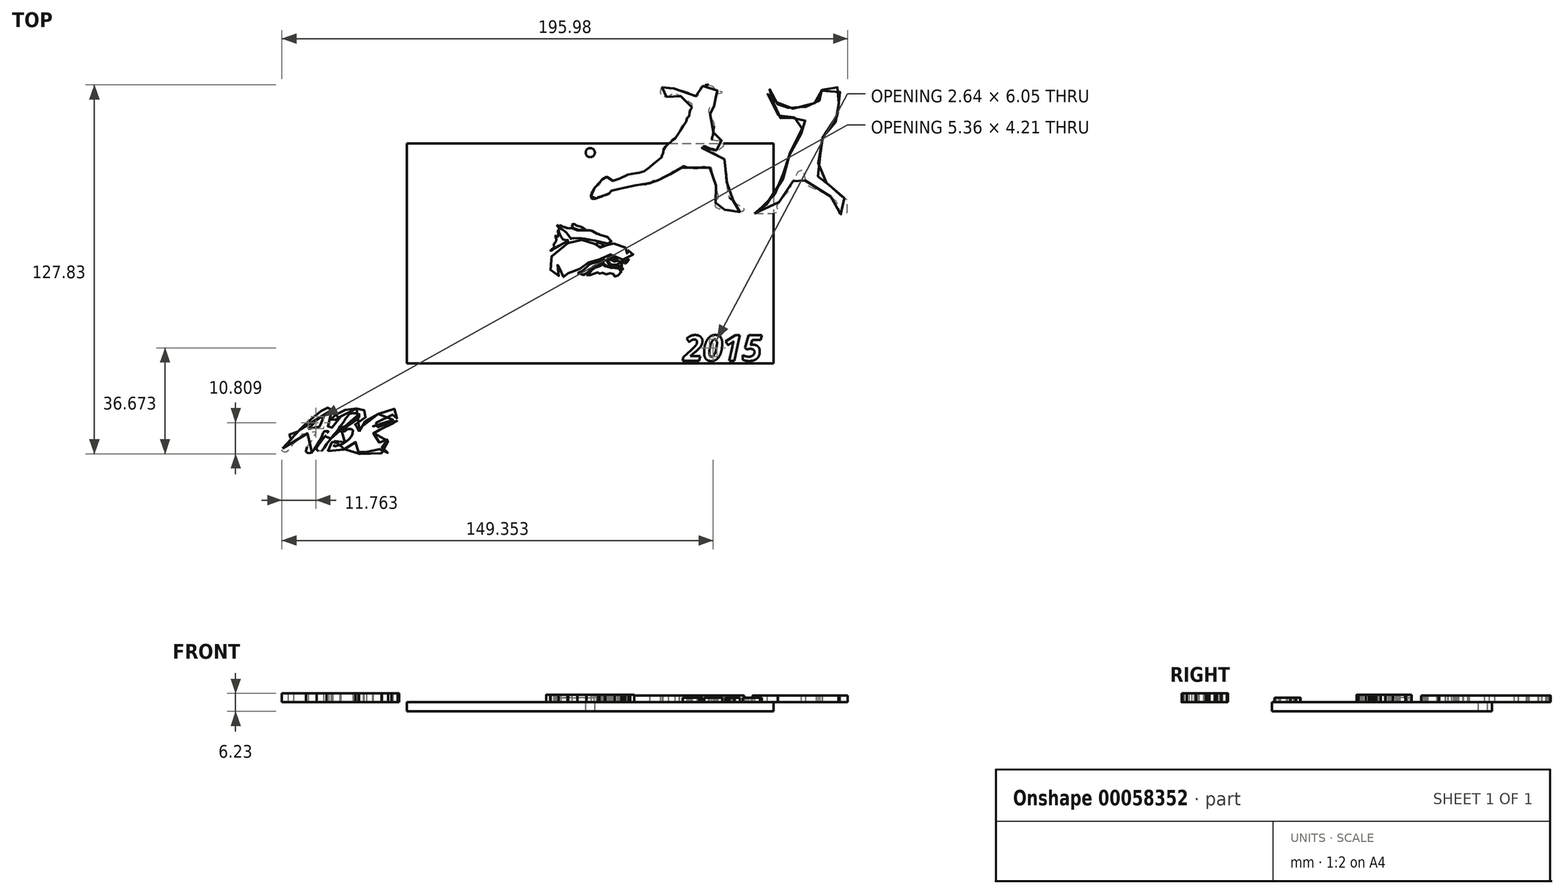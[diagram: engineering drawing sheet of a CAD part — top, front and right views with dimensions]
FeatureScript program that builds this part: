
annotation { "Feature Type Name" : "Feature", "Feature Type Description" : "" }
export const myFeature = defineFeature(function(context is Context, id is Id, definition is map)
    precondition{}
    {
        {
            var Q0;
            Q0=qCreatedBy(makeId("Top.planeOp"),FACE);
            var sketch = newSketch(context, id + "F0", { "sketchPlane" : qUnion([Q0])});
            skFitSpline(sketch, "E0", {"points": [v(-30.29, 18.5) * mm, v(-33.5, 18.37) * mm, v(-36.8, 18.87) * mm, v(-39.5, 22) * mm, v(-42.22, 26.8) * mm, v(-43.58, 30.51) * mm, v(-43.65, 32.58) * mm, v(-43.94, 32.87) * mm, v(-44.5, 32.87) * mm, v(-44.44, 31.3) * mm, v(-44.22, 23) * mm, v(-44.44, 22.72) * mm, v(-45.3, 23.3) * mm, v(-47.3, 24.5) * mm, v(-48.36, 24.87) * mm, v(-48.22, 23.58) * mm, v(-48.22, 21.87) * mm, v(-46.94, 20.08) * mm, v(-45.86, 19.3) * mm, v(-50.65, 12.94) * mm, v(-50.72, 12) * mm, v(-50.5, 10.86) * mm, v(-50, 10.08) * mm, v(-49.58, 9.15) * mm, v(-49.86, 8.65) * mm, v(-51.87, 7) * mm, v(-54.65, 4.8) * mm, v(-55.3, 3.86) * mm, v(-55.08, 3.3) * mm, v(-54.37, 3.15) * mm, v(-53.22, 4.58) * mm, v(-47.65, 8.15) * mm, v(-38.8, 12.86) * mm, v(-32.3, 16.37) * mm, v(-30.22, 17.3) * mm, v(-30.29, 18.5) * mm]});
            skFitSpline(sketch, "E1", {"points": [v(-45.56, 38.1) * mm, v(-39.19, 33.33) * mm, v(-33.89, 30.17) * mm, v(-33.2, 29.53) * mm, v(-32.34, 28.09) * mm, v(-27.47, 21.24) * mm, v(-26.61, 20.27) * mm, v(-25.17, 20.49) * mm, v(-18.42, 21.13) * mm, v(-14.2, 21.18) * mm, v(-7.5, 20.17) * mm, v(5.34, 17.86) * mm, v(14.44, 15.94) * mm, v(23.65, 13.64) * mm, v(24.13, 13.48) * mm, v(24.98, 14.01) * mm, v(27.55, 15.35) * mm, v(28.78, 16.2) * mm, v(28.94, 17) * mm, v(28.2, 17.92) * mm, v(26.54, 19.74) * mm, v(24.82, 21.66) * mm, v(24.23, 22.36) * mm, v(23.16, 22.84) * mm, v(15.46, 24.93) * mm, v(12.25, 26.43) * mm, v(8.77, 27.71) * mm, v(5.02, 29.96) * mm, v(2.72, 31.14) * mm, v(0.58, 31.67) * mm, v(-0.97, 31.94) * mm, v(-11.04, 31.83) * mm, v(-16.17, 31.78) * mm, v(-17.14, 31.67) * mm, v(-17.94, 32.05) * mm, v(-21.42, 33.39) * mm, v(-25.06, 34.62) * mm, v(-25.86, 34.94) * mm, v(-33.03, 35) * mm, v(-35.17, 36.06) * mm, v(-37.2, 36.97) * mm, v(-39.78, 38.1) * mm, v(-42.5, 38.52) * mm, v(-44.65, 38.8) * mm, v(-45.5, 38.8) * mm, v(-45.56, 38.1) * mm]});
            skFitSpline(sketch, "E2", {"points": [v(-25.5, 39.45) * mm, v(-23.8, 35.5) * mm, v(-23.6, 34.96) * mm, v(-23.33, 34.6) * mm, v(-22.32, 34.5) * mm, v(-20.87, 34.29) * mm, v(-19.32, 33.82) * mm, v(-17, 32.8) * mm, v(-16.66, 32.64) * mm, v(-10.29, 32.57) * mm, v(-6.4, 32.74) * mm, v(-7.55, 33.78) * mm, v(-9.88, 35.44) * mm, v(-12.4, 36.65) * mm, v(-15.28, 37.53) * mm, v(-17.5, 38.13) * mm, v(-19.25, 38.64) * mm, v(-20.47, 39.55) * mm, v(-22.29, 40.72) * mm, v(-24.82, 40.36) * mm, v(-25.5, 39.95) * mm, v(-25.5, 39.45) * mm]});
            skFitSpline(sketch, "E3", {"points": [v(9.56, 14.74) * mm, v(8.97, 13.48) * mm, v(9.05, 12.11) * mm, v(10.1, 10.97) * mm, v(11.96, 9.82) * mm, v(13.28, 9.39) * mm, v(15.02, 9.41) * mm, v(15.96, 9.87) * mm, v(16.9, 10.71) * mm, v(18.18, 11.63) * mm, v(18.5, 12.04) * mm, v(18.53, 12.75) * mm, v(17.31, 13.08) * mm, v(12.77, 14.38) * mm, v(10.8, 15.05) * mm, v(10.02, 15.07) * mm, v(9.56, 14.74) * mm]});
            skFitSpline(sketch, "E4", {"points": [v(-17.1, -27.56) * mm, v(-14.32, -28.36) * mm, v(-10.42, -29.66) * mm, v(-9.47, -30) * mm, v(-8.36, -29.36) * mm, v(-5.11, -27.03) * mm, v(-3.7, -26.1) * mm, v(-1.71, -24.39) * mm, v(1.04, -21.14) * mm, v(2.6, -19.5) * mm, v(4.48, -18.2) * mm, v(8.18, -16.48) * mm, v(11.2, -15.6) * mm, v(13.42, -14.95) * mm, v(16.82, -13.3) * mm, v(16.9, -11.82) * mm, v(17.12, -10.02) * mm, v(17.89, -8.3) * mm, v(18.46, -7.46) * mm, v(17.39, -7.85) * mm, v(16.2, -8.76) * mm, v(14.6, -9.87) * mm, v(7.8, -12.43) * mm, v(2.34, -13.8) * mm, v(-0.68, -15.03) * mm, v(-3.43, -17.63) * mm, v(-7.79, -21.49) * mm, v(-10.58, -23.59) * mm, v(-14.93, -25.92) * mm, v(-17.6, -26.83) * mm, v(-17.1, -27.56) * mm]});
            skFitSpline(sketch, "E5", {"points": [v(23.75, -4.13) * mm, v(24.48, -3.2) * mm, v(25.16, -3.08) * mm, v(26.69, -2.9) * mm, v(28.06, -2.89) * mm, v(29.84, -3.32) * mm, v(32.15, -4.32) * mm, v(34.8, -5.67) * mm, v(37.04, -6.9) * mm, v(37.75, -7.35) * mm, v(37.56, -7.75) * mm, v(36.27, -8.6) * mm, v(35.24, -9) * mm, v(33.8, -8.72) * mm, v(32.37, -8.25) * mm, v(31.43, -7.95) * mm, v(31.25, -7.13) * mm, v(31.15, -6.36) * mm, v(31.15, -5.14) * mm, v(30.8, -5.42) * mm, v(30.14, -6) * mm, v(29.88, -6.36) * mm, v(29.28, -6.34) * mm, v(27.8, -6.36) * mm, v(27.07, -6.34) * mm, v(27.1, -5.97) * mm, v(27.2, -5.35) * mm, v(27.48, -4.56) * mm, v(27.63, -3.85) * mm, v(26.56, -3.87) * mm, v(24.78, -4.17) * mm, v(23.75, -4.13) * mm]});
            skFitSpline(sketch, "E6", {"points": [v(42.3, -15.24) * mm, v(43.14, -12.43) * mm, v(44, -9.41) * mm, v(44.24, -9.4) * mm, v(46.02, -9.52) * mm, v(48.6, -9.68) * mm, v(50.5, -9.46) * mm, v(51.99, -8.83) * mm, v(53.36, -8.48) * mm, v(53.14, -8.89) * mm, v(51.38, -11.46) * mm, v(50.37, -12.5) * mm, v(49.3, -13.46) * mm, v(47.98, -14.1) * mm, v(47.94, -13.77) * mm, v(48.02, -12.17) * mm, v(48.08, -10.9) * mm, v(47.84, -10.97) * mm, v(46.36, -12.39) * mm, v(43.91, -14.31) * mm, v(42.3, -15.24) * mm]});
            skFitSpline(sketch, "E7", {"points": [v(43.59, -15.91) * mm, v(42.43, -17.19) * mm, v(42.33, -17.35) * mm, v(42.48, -17.57) * mm, v(43.59, -18.48) * mm, v(43.75, -18.58) * mm, v(43.77, -18.3) * mm, v(43.77, -16.05) * mm, v(43.75, -15.86) * mm, v(43.59, -15.91) * mm]});
            skFitSpline(sketch, "E8", {"points": [v(39.9, -15.52) * mm, v(40.03, -16.05) * mm, v(40.03, -17.43) * mm, v(39.79, -18.75) * mm, v(39.3, -19.6) * mm, v(38.94, -19.62) * mm, v(37.16, -19.62) * mm, v(36.97, -19.6) * mm, v(37.16, -19.2) * mm, v(39.64, -15.72) * mm, v(39.9, -15.52) * mm]});
            skFitSpline(sketch, "E9", {"points": [v(41.04, -17.52) * mm, v(40.6, -19.86) * mm, v(40.58, -20.2) * mm, v(40.94, -20.3) * mm, v(41.42, -20.36) * mm, v(42.17, -20.96) * mm, v(43.1, -21.76) * mm, v(43.54, -22.48) * mm, v(43.78, -22.82) * mm, v(44.22, -22.62) * mm, v(45.2, -22.02) * mm, v(45.56, -21.78) * mm, v(45.4, -21.42) * mm, v(43.85, -19.47) * mm, v(42.58, -18.41) * mm, v(41.47, -17.62) * mm, v(41.04, -17.52) * mm]});
            skFitSpline(sketch, "E10", {"points": [v(23.28, -8.71) * mm, v(24.22, -9.48) * mm, v(25, -10.64) * mm, v(25.95, -12.13) * mm, v(26.6, -13.31) * mm, v(27.4, -14.2) * mm, v(28.72, -15) * mm, v(29.97, -15.52) * mm, v(32.5, -15.81) * mm, v(35.48, -15.62) * mm, v(37.62, -15.28) * mm, v(38.1, -15.21) * mm, v(38.49, -14.78) * mm, v(38.97, -14.27) * mm, v(39.02, -13.82) * mm, v(39.64, -13.26) * mm, v(40.32, -12.9) * mm, v(41.01, -12.37) * mm, v(41.6, -11.58) * mm, v(41.16, -11.34) * mm, v(37.98, -10.3) * mm, v(37.3, -10.13) * mm, v(36.37, -10.42) * mm, v(35, -10.93) * mm, v(34.1, -11.31) * mm, v(33.5, -11.31) * mm, v(32.71, -10.93) * mm, v(32.33, -10.78) * mm, v(29.77, -9.68) * mm, v(27.85, -8.71) * mm, v(26.3, -8.06) * mm, v(25, -7.8) * mm, v(23.78, -7.65) * mm, v(23.13, -7.7) * mm, v(22.9, -8.16) * mm, v(23.28, -8.71) * mm]});
            skFitSpline(sketch, "E11", {"points": [v(37.12, -17.57) * mm, v(36.2, -18.77) * mm, v(36, -19.06) * mm, v(35.65, -19.01) * mm, v(33.31, -19) * mm, v(30.14, -18.85) * mm, v(27.56, -18.41) * mm, v(24.65, -17.84) * mm, v(22.36, -16.92) * mm, v(20.39, -15.74) * mm, v(19.35, -14.61) * mm, v(18.56, -13.2) * mm, v(18.15, -11.77) * mm, v(18.22, -10.25) * mm, v(18.6, -9.72) * mm, v(19.64, -9.2) * mm, v(20.97, -9.12) * mm, v(22.53, -10.1) * mm, v(23.61, -11.58) * mm, v(24.5, -13.36) * mm, v(25.76, -15.48) * mm, v(27.2, -16.44) * mm, v(28.9, -17.11) * mm, v(31.03, -17.5) * mm, v(33.8, -17.55) * mm, v(36.47, -17.6) * mm, v(37.12, -17.57) * mm]});
            skFitSpline(sketch, "E12", {"points": [v(-5.34, -30.01) * mm, v(-4.04, -29.3) * mm, v(-1.91, -27.92) * mm, v(-0.65, -27.02) * mm, v(1.3, -24.68) * mm, v(2.41, -23.09) * mm, v(3.79, -21.43) * mm, v(4.8, -20.5) * mm, v(7.54, -19.23) * mm, v(10.28, -18.5) * mm, v(12.8, -17.86) * mm, v(14.82, -17.21) * mm, v(16.33, -16.24) * mm, v(17.63, -15.12) * mm, v(18.1, -15.37) * mm, v(19.54, -16.63) * mm, v(23.37, -18.5) * mm, v(27.08, -19.66) * mm, v(31.16, -20.24) * mm, v(33.54, -20.35) * mm, v(36.06, -20.5) * mm, v(38.08, -20.78) * mm, v(41.04, -21.68) * mm, v(42.44, -23.38) * mm, v(42.84, -25.69) * mm, v(41.76, -28.03) * mm, v(39.56, -29.83) * mm, v(36.13, -31.53) * mm, v(33.82, -32.57) * mm, v(33.97, -31.96) * mm, v(34.04, -30.37) * mm, v(33.5, -29.22) * mm, v(32.24, -28.4) * mm, v(30.43, -27.78) * mm, v(29.68, -27.74) * mm, v(27.44, -27.34) * mm, v(25.2, -27.74) * mm, v(22.93, -28.4) * mm, v(21.56, -29.22) * mm, v(21.2, -29.8) * mm, v(20.48, -29.76) * mm, v(20.52, -29.11) * mm, v(20.3, -27.85) * mm, v(19.54, -27.13) * mm, v(18.07, -26.77) * mm, v(16.66, -26.73) * mm, v(15.32, -27.02) * mm, v(13.74, -27.63) * mm, v(12.48, -28.35) * mm, v(11.61, -28.75) * mm, v(11.29, -28.5) * mm, v(11.47, -28) * mm, v(12.04, -27.3) * mm, v(12.48, -26.8) * mm, v(12.37, -26.37) * mm, v(11.75, -26.12) * mm, v(10.7, -26.15) * mm, v(9.7, -26.33) * mm, v(8.18, -26.84) * mm, v(5.4, -27.92) * mm, v(3, -28.9) * mm, v(0.61, -29.76) * mm, v(-1.44, -30.09) * mm, v(-4.18, -30.34) * mm, v(-5.34, -30.01) * mm]});
            skFitSpline(sketch, "E13", {"points": [v(-53.65, -9.02) * mm, v(-54.94, -12.28) * mm, v(-55.45, -15.2) * mm, v(-55.62, -18.54) * mm, v(-55.45, -21.37) * mm, v(-54.5, -23.77) * mm, v(-51.76, -26.7) * mm, v(-49.45, -28.58) * mm, v(-46.02, -30.38) * mm, v(-43.7, -31.32) * mm, v(-44.05, -30.38) * mm, v(-45.67, -26.95) * mm, v(-46.62, -23.26) * mm, v(-46.79, -19.23) * mm, v(-45.16, -15.45) * mm, v(-43.53, -13.74) * mm, v(-41.73, -12.2) * mm, v(-40.96, -11.77) * mm, v(-41.64, -13.74) * mm, v(-43.27, -19.14) * mm, v(-43.7, -23.43) * mm, v(-42.84, -26.7) * mm, v(-40.87, -29.7) * mm, v(-38.04, -32.18) * mm, v(-35.04, -33.8) * mm, v(-30.75, -35.48) * mm, v(-31.27, -34.32) * mm, v(-31.7, -31.66) * mm, v(-30.75, -27.98) * mm, v(-28.86, -25.49) * mm, v(-24.32, -23.95) * mm, v(-18.31, -22.66) * mm, v(-14.28, -21.37) * mm, v(-12.83, -20.43) * mm, v(-11.02, -18.46) * mm, v(-8.2, -15.88) * mm, v(-4.76, -13.48) * mm, v(-1.08, -12.1) * mm, v(2.96, -11.08) * mm, v(7.33, -10.14) * mm, v(10.85, -9.1) * mm, v(13.85, -7.56) * mm, v(17.1, -5.25) * mm, v(19.94, -3.28) * mm, v(22.77, -1.47) * mm, v(28.51, -1.39) * mm, v(32.2, -2.68) * mm, v(38.12, -5.33) * mm, v(43.18, -7.74) * mm, v(47.04, -8.68) * mm, v(50.39, -8.34) * mm, v(55.19, -6.45) * mm, v(58.02, -3.96) * mm, v(60.44, 0.75) * mm, v(60.82, 2.12) * mm, v(59.83, 2.66) * mm, v(55.54, 4.5) * mm, v(53.37, 5.11) * mm, v(53.12, 4.79) * mm, v(52.76, 3.5) * mm, v(52.11, 1.5) * mm, v(52.3, 1.11) * mm, v(54.93, -1.09) * mm, v(55.14, -1.49) * mm, v(55.1, -1.63) * mm, v(54.7, -1.3) * mm, v(51, 0) * mm, v(51.07, 0.64) * mm, v(51.35, 3.27) * mm, v(51.54, 5.44) * mm, v(51.79, 6.38) * mm, v(51.46, 7.02) * mm, v(50.96, 7.53) * mm, v(49.73, 7.78) * mm, v(43.02, 9.15) * mm, v(37.47, 10.52) * mm, v(35.42, 11.6) * mm, v(33.14, 12.87) * mm, v(30.87, 14.7) * mm, v(30.26, 15.07) * mm, v(29.65, 14.85) * mm, v(28.7, 14.13) * mm, v(25.54, 11.53) * mm, v(25.17, 11.24) * mm, v(24.67, 11.2) * mm, v(23.48, 11.71) * mm, v(22, 12.15) * mm, v(21.64, 12.22) * mm, v(20.96, 11.68) * mm, v(19.4, 10.13) * mm, v(17.13, 9) * mm, v(14.97, 8.1) * mm, v(11, 8.03) * mm, v(8.12, 8.86) * mm, v(6.06, 10.52) * mm, v(5.09, 11.46) * mm, v(4.87, 11.9) * mm, v(5.09, 12.25) * mm, v(7.04, 14.16) * mm, v(8, 15.14) * mm, v(8.23, 15.46) * mm, v(7.76, 15.68) * mm, v(-7.9, 18.1) * mm, v(-15.86, 18.85) * mm, v(-22.35, 18.89) * mm, v(-26, 17.77) * mm, v(-34.22, 11.96) * mm, v(-41.25, 6.3) * mm, v(-52.68, -3.25) * mm, v(-60.18, -9.64) * mm, v(-61.23, -10.65) * mm, v(-60.4, -10.6) * mm, v(-54.16, -9.02) * mm, v(-53.65, -9.02) * mm]});
            skSolve(sketch);
        }
        {
            var Q0;
            Q0 = qSketchRegion(id + "F0", true);
            extrude(context, id + "F1", {"entities" : qUnion([Q0]), "depth" : 10.16 * mm});
        }
        {
            var Q0;
            Q0=makeQuery(id+"F1.opExtrude","SWEPT_BODY",BODY,{"disambiguationData":[OSD([sQuery(id+"F0.wireOp",EDGE,"E8")])]});
            var Q1;
            Q1=makeQuery(id+"F1.opExtrude","SWEPT_BODY",BODY,{"disambiguationData":[OSD([sQuery(id+"F0.wireOp",EDGE,"E13")])]});
            var Q2;
            Q2=makeQuery(id+"F1.opExtrude","SWEPT_BODY",BODY,{"disambiguationData":[OSD([sQuery(id+"F0.wireOp",EDGE,"E9")])]});
            var Q3;
            Q3=makeQuery(id+"F1.opExtrude","SWEPT_BODY",BODY,{"disambiguationData":[OSD([sQuery(id+"F0.wireOp",EDGE,"E12")])]});
            var Q4;
            Q4=makeQuery(id+"F1.opExtrude","SWEPT_BODY",BODY,{"disambiguationData":[OSD([sQuery(id+"F0.wireOp",EDGE,"E6")])]});
            var Q5;
            Q5=makeQuery(id+"F1.opExtrude","SWEPT_BODY",BODY,{"disambiguationData":[OSD([sQuery(id+"F0.wireOp",EDGE,"E10")])]});
            var Q6;
            Q6=makeQuery(id+"F1.opExtrude","SWEPT_BODY",BODY,{"disambiguationData":[OSD([sQuery(id+"F0.wireOp",EDGE,"E7")])]});
            var Q7;
            Q7=makeQuery(id+"F1.opExtrude","SWEPT_BODY",BODY,{"disambiguationData":[OSD([sQuery(id+"F0.wireOp",EDGE,"E11")])]});
            var Q8;
            Q8=makeQuery(id+"F1.opExtrude","SWEPT_BODY",BODY,{"disambiguationData":[OSD([sQuery(id+"F0.wireOp",EDGE,"E5")])]});
            var Q9;
            Q9=makeQuery(id+"F1.opExtrude","SWEPT_BODY",BODY,{"disambiguationData":[OSD([sQuery(id+"F0.wireOp",EDGE,"E4")])]});
            var Q10;
            Q10=makeQuery(id+"F1.opExtrude","SWEPT_BODY",BODY,{"disambiguationData":[OSD([sQuery(id+"F0.wireOp",EDGE,"E0")])]});
            var Q11;
            Q11=makeQuery(id+"F1.opExtrude","SWEPT_BODY",BODY,{"disambiguationData":[OSD([sQuery(id+"F0.wireOp",EDGE,"E1")])]});
            var Q12;
            Q12=makeQuery(id+"F1.opExtrude","SWEPT_BODY",BODY,{"disambiguationData":[OSD([sQuery(id+"F0.wireOp",EDGE,"E2")])]});
            var Q13;
            Q13=makeQuery(id+"F1.opExtrude","SWEPT_BODY",BODY,{"disambiguationData":[OSD([sQuery(id+"F0.wireOp",EDGE,"E3")])]});
            var Q14;
            Q14=makeQuery(id+"F4.opExtrude","SWEPT_BODY",BODY,{"disambiguationData":[OSD([sQuery(id+"F3.wireOp",EDGE,"E14.bottom"),sQuery(id+"F3.wireOp",EDGE,"E14.top"),sQuery(id+"F3.wireOp",EDGE,"E14.left"),sQuery(id+"F3.wireOp",EDGE,"E14.right")])]});
            var Q15;
            Q15=qCreatedBy(makeId("Origin.pointOp"),VERTEX);
            transform(context, id + "F2", {"entities" : qUnion([Q0, Q1, Q2, Q3, Q4, Q5, Q6, Q7, Q8, Q9, Q10, Q11, Q12, Q13, Q14]), "transformType" : TransformType.SCALE_UNIFORMLY, "scale" : .25, "scalePoint" : qUnion([Q15]), "makeCopy" : false});
        }
        {
            var Q0;
            Q0=qCreatedBy(makeId("Top.planeOp"),FACE);
            var sketch = newSketch(context, id + "F3", { "sketchPlane" : qUnion([Q0])});
            skLineSegment(sketch, "E14.bottom", {"start": v(-63.5, 38.1) * mm, "end": v(63.5, 38.1) * mm});
            skLineSegment(sketch, "E14.top", {"start": v(-63.5, -38.1) * mm, "end": v(63.5, -38.1) * mm});
            skLineSegment(sketch, "E14.left", {"start": v(-63.5, 38.1) * mm, "end": v(-63.5, -38.1) * mm});
            skLineSegment(sketch, "E14.right", {"start": v(63.5, 38.1) * mm, "end": v(63.5, -38.1) * mm});
            skSolve(sketch);
        }
        {
            var Q0;
            Q0 = qSketchRegion(id + "F3", true);
            extrude(context, id + "F4", {"entities" : qUnion([Q0]), "oppositeDirection" : true, "depth" : 3.17 * mm});
        }
        {
            var Q0;
            Q0=makeQuery(id+"F4.opExtrude","CAP_FACE",FACE,{"disambiguationData":[OSD([sQuery(id+"F3.wireOp",EDGE,"E14.bottom"),sQuery(id+"F3.wireOp",EDGE,"E14.top"),sQuery(id+"F3.wireOp",EDGE,"E14.left"),sQuery(id+"F3.wireOp",EDGE,"E14.right")])],"isStart":true});
            var sketch = newSketch(context, id + "F5", { "sketchPlane" : qUnion([Q0])});
            skText(sketch, "E15", { "text": "2015", "fontName": "OpenSans-BoldItalic.ttf"});
            const initialGuessF5  = {"E15": [0.03224, -0.03717, 1, 0, 0.00887]};
            skSetInitialGuess(sketch, initialGuessF5);
            skSolve(sketch);
        }
        {
            var Q0;
            Q0 = qSketchRegion(id + "F5", true);
            extrude(context, id + "F6", {"entities" : qUnion([Q0]), "depth" : 1.52 * mm});
        }
        {
            var Q0;
            {var subQ2=sQuery(id+"F3.wireOp",EDGE,"E14.bottom");var subQ30=sQuery(id+"F3.wireOp",EDGE,"E14.top");var subQ31=sQuery(id+"F3.wireOp",EDGE,"E14.left");var subQ32=sQuery(id+"F3.wireOp",EDGE,"E14.right");Q0=makeQuery(id+"F6.boolean.opBoolean","SPLIT",FACE,{"disambiguationData":[TD([makeQuery(id+"F4.opExtrude","SWEPT_FACE",FACE,{"disambiguationData":[OSD([subQ2])]})])],"derivedFrom":makeQuery(id+"F4.opExtrude","CAP_FACE",FACE,{"disambiguationData":[OSD([subQ2,subQ30,subQ31,subQ32])],"isStart":true})});}
            var sketch = newSketch(context, id + "F7", { "sketchPlane" : qUnion([Q0])});
            skFitSpline(sketch, "E16", {"points": [v(37.93, 9.27) * mm, v(42.72, 9.27) * mm, v(43.15, 9.29) * mm, v(43.33, 9.51) * mm, v(43.3, 10.19) * mm, v(43.15, 10.7) * mm, v(43.08, 11.16) * mm, v(43.26, 11.47) * mm, v(44.23, 12.62) * mm, v(45.15, 13.68) * mm, v(45.47, 14.04) * mm, v(45.96, 14.35) * mm, v(46.19, 14.9) * mm, v(46.35, 15.43) * mm, v(46.46, 15.93) * mm, v(46.62, 16.35) * mm, v(47.2, 17.19) * mm, v(47.43, 17.57) * mm, v(47.56, 18.18) * mm, v(48.96, 19.9) * mm, v(49.11, 19.48) * mm, v(49.36, 18.22) * mm, v(49.6, 16.94) * mm, v(49.97, 15.95) * mm, v(50.44, 15.5) * mm, v(51.05, 15.2) * mm, v(51.88, 14.91) * mm, v(52.96, 14.44) * mm, v(54.47, 13.74) * mm, v(56.13, 12.73) * mm, v(56.56, 12.28) * mm, v(57.1, 11.45) * mm, v(57.33, 10.75) * mm, v(57.44, 10.17) * mm, v(57.46, 9.63) * mm, v(57.3, 9.24) * mm, v(57.33, 9.1) * mm, v(57.53, 9.06) * mm, v(57.98, 9.04) * mm, v(58.83, 9.13) * mm, v(59.26, 9.38) * mm, v(59.44, 9.78) * mm, v(59.44, 10.26) * mm, v(59.33, 11.11) * mm, v(59.24, 11.56) * mm, v(59.28, 12.42) * mm, v(58.77, 12.75) * mm, v(58.27, 13.05) * mm, v(57.82, 13.11) * mm, v(57.5, 13.14) * mm, v(57.01, 13.6) * mm, v(56.52, 14.2) * mm, v(55.82, 15.07) * mm, v(55.28, 15.72) * mm, v(54.76, 16.2) * mm, v(54.18, 16.62) * mm, v(53.64, 16.96) * mm, v(53.14, 17.14) * mm, v(52.9, 17.19) * mm, v(52.6, 17.34) * mm, v(52.58, 17.77) * mm, v(52.58, 18.72) * mm, v(52.6, 20.09) * mm, v(52.62, 20.92) * mm, v(52.74, 21.6) * mm, v(53.05, 22.52) * mm, v(53.46, 23.2) * mm, v(53.55, 23.87) * mm, v(53.5, 24.8) * mm, v(53.55, 25.62) * mm, v(53.55, 26.37) * mm, v(53.8, 26.9) * mm, v(54.85, 27.63) * mm, v(55.55, 28.3) * mm, v(56.2, 29.16) * mm, v(56.56, 29.79) * mm, v(56.7, 30.62) * mm, v(57.01, 31.84) * mm, v(57.46, 32.65) * mm, v(57.62, 33.3) * mm, v(57.6, 33.84) * mm, v(57.46, 34.54) * mm, v(57.3, 34.9) * mm, v(57.57, 35.53) * mm, v(57.75, 36.22) * mm, v(57.7, 37.17) * mm, v(57.48, 37.87) * mm, v(57.12, 38.32) * mm, v(56.7, 38.65) * mm, v(56.13, 38.83) * mm, v(55.4, 38.83) * mm, v(54.45, 38.65) * mm, v(53.9, 38.34) * mm, v(53.48, 37.78) * mm, v(53.25, 37.24) * mm, v(53.12, 36.92) * mm, v(52.8, 36.8) * mm, v(52.26, 36.47) * mm, v(52.2, 36.13) * mm, v(52.51, 35.82) * mm, v(52.78, 35.44) * mm, v(52.98, 35.23) * mm, v(52.53, 35) * mm, v(51.95, 34.76) * mm, v(51.27, 34.29) * mm, v(50.9, 34.09) * mm, v(50.37, 34.02) * mm, v(49.83, 33.86) * mm, v(49.16, 33.64) * mm, v(48.66, 33.41) * mm, v(48.28, 33.25) * mm, v(47.4, 33.3) * mm, v(46.57, 33.46) * mm, v(45.9, 33.57) * mm, v(45.24, 33.66) * mm, v(44.8, 33.8) * mm, v(44.57, 33.9) * mm, v(44.16, 33.93) * mm, v(43.94, 33.82) * mm, v(43.76, 33.43) * mm, v(43.4, 34.13) * mm, v(43.06, 34.96) * mm, v(42.9, 35.75) * mm, v(42.59, 36.43) * mm, v(42.32, 37.01) * mm, v(41.89, 37.57) * mm, v(41.62, 37.84) * mm, v(41.12, 37.87) * mm, v(40.92, 37.66) * mm, v(40.8, 37.33) * mm, v(40.92, 36.88) * mm, v(41.35, 36) * mm, v(42, 35.1) * mm, v(42.77, 34.04) * mm, v(43.17, 33.43) * mm, v(43.44, 32.96) * mm, v(43.4, 32.74) * mm, v(43.3, 32.4) * mm, v(43.42, 32.02) * mm, v(43.78, 31.4) * mm, v(44.1, 30.98) * mm, v(44.48, 30.46) * mm, v(45.15, 30.53) * mm, v(45.4, 30.76) * mm, v(45.74, 31) * mm, v(46.03, 31.1) * mm, v(46.35, 31.3) * mm, v(46.64, 31.36) * mm, v(46.95, 31.36) * mm, v(47.54, 31.48) * mm, v(48.06, 31.34) * mm, v(48.69, 31.3) * mm, v(49.2, 31.12) * mm, v(49.65, 30.9) * mm, v(49.59, 30.62) * mm, v(49.38, 30.2) * mm, v(49.18, 29.79) * mm, v(49.02, 29.1) * mm, v(48.91, 28.73) * mm, v(48.7, 28.5) * mm, v(48.69, 28.17) * mm, v(48.69, 27.74) * mm, v(48.48, 27.15) * mm, v(48.28, 26.68) * mm, v(47.74, 25.94) * mm, v(46.62, 24.48) * mm, v(45.9, 22.5) * mm, v(45.47, 20.85) * mm, v(45.33, 19.84) * mm, v(45.09, 19.4) * mm, v(44.82, 18.99) * mm, v(44.6, 18.51) * mm, v(44.55, 17.9) * mm, v(44.5, 17.3) * mm, v(44.41, 16.92) * mm, v(44.07, 16.4) * mm, v(43.15, 14.73) * mm, v(42.23, 13.05) * mm, v(41.69, 12.28) * mm, v(40.97, 11.54) * mm, v(40.52, 11.25) * mm, v(40.11, 11.11) * mm, v(39.84, 10.93) * mm, v(39.6, 10.6) * mm, v(39.21, 10.35) * mm, v(38.6, 10.3) * mm, v(37.93, 10.19) * mm, v(37.61, 10) * mm, v(37.5, 9.78) * mm, v(37.5, 9.42) * mm, v(37.93, 9.27) * mm]});
            skSolve(sketch);
        }
        {
            var Q0;
            Q0 = qSketchRegion(id + "F7", true);
            extrude(context, id + "F8", {"entities" : qUnion([Q0]), "depth" : 1.52 * mm});
        }
        {
            var Q0;
            {var subQ2=sQuery(id+"F3.wireOp",EDGE,"E14.bottom");var subQ30=sQuery(id+"F3.wireOp",EDGE,"E14.top");var subQ31=sQuery(id+"F3.wireOp",EDGE,"E14.left");var subQ32=sQuery(id+"F3.wireOp",EDGE,"E14.right");Q0=makeQuery(id+"F6.boolean.opBoolean","SPLIT",FACE,{"disambiguationData":[TD([makeQuery(id+"F4.opExtrude","SWEPT_FACE",FACE,{"disambiguationData":[OSD([subQ2])]})])],"derivedFrom":makeQuery(id+"F4.opExtrude","CAP_FACE",FACE,{"disambiguationData":[OSD([subQ2,subQ30,subQ31,subQ32])],"isStart":true})});}
            var sketch = newSketch(context, id + "F9", { "sketchPlane" : qUnion([Q0])});
            skFitSpline(sketch, "E17", {"points": [v(-53.3, -33.77) * mm, v(-52.38, -32.7) * mm, v(-51.4, -31.76) * mm, v(-51.62, -31.77) * mm, v(-51.92, -31.86) * mm, v(-52.22, -31.88) * mm, v(-52.33, -31.77) * mm, v(-52.26, -31.52) * mm, v(-52, -31.29) * mm, v(-51.58, -31.17) * mm, v(-50.53, -30.84) * mm, v(-50.47, -30.73) * mm, v(-49.87, -30.14) * mm, v(-48.84, -29.11) * mm, v(-47.58, -28.04) * mm, v(-46.88, -27.5) * mm, v(-46.26, -27.1) * mm, v(-45.84, -26.88) * mm, v(-45.4, -26.7) * mm, v(-45.2, -26.7) * mm, v(-44.85, -26.81) * mm, v(-44.7, -27.06) * mm, v(-44.8, -27.72) * mm, v(-45.27, -29.07) * mm, v(-45.65, -29.96) * mm, v(-45.5, -29.96) * mm, v(-45.33, -29.95) * mm, v(-45.1, -29.95) * mm, v(-44.87, -30.02) * mm, v(-44.76, -30.17) * mm, v(-44.65, -30.03) * mm, v(-43.22, -28.29) * mm, v(-43.3, -28.26) * mm, v(-43.8, -28.56) * mm, v(-44.27, -28.88) * mm, v(-44.7, -29.1) * mm, v(-44.9, -29.02) * mm, v(-44.9, -28.75) * mm, v(-44.78, -28.4) * mm, v(-44.4, -28.11) * mm, v(-43.42, -27.53) * mm, v(-42.42, -27.14) * mm, v(-41.18, -26.9) * mm, v(-40.18, -26.88) * mm, v(-39.4, -27.02) * mm, v(-39.05, -27.23) * mm, v(-38.78, -27.61) * mm, v(-38.9, -28.35) * mm, v(-39.49, -28.98) * mm, v(-40.97, -29.83) * mm, v(-40.85, -29.84) * mm, v(-40.7, -29.88) * mm, v(-40.47, -29.95) * mm, v(-40.2, -30.11) * mm, v(-39.99, -30.45) * mm, v(-40, -30.86) * mm, v(-39.85, -30.67) * mm, v(-39.38, -30.02) * mm, v(-39.2, -29.76) * mm, v(-39.28, -29.54) * mm, v(-39.2, -29.2) * mm, v(-39, -29.06) * mm, v(-38.66, -29.06) * mm, v(-38.46, -29.14) * mm, v(-38.23, -28.9) * mm, v(-37.53, -28.33) * mm, v(-36.66, -27.81) * mm, v(-35.99, -27.46) * mm, v(-35.34, -27.14) * mm, v(-34.77, -26.96) * mm, v(-33.99, -26.9) * mm, v(-33.5, -27.02) * mm, v(-33.18, -27.23) * mm, v(-33.14, -27.76) * mm, v(-33.27, -28.38) * mm, v(-33.4, -28.57) * mm, v(-33.62, -28.58) * mm, v(-34.24, -28.92) * mm, v(-34.4, -29) * mm, v(-34.3, -28.76) * mm, v(-34.15, -28.38) * mm, v(-34.19, -28) * mm, v(-34.31, -27.9) * mm, v(-34.82, -27.87) * mm, v(-35.65, -28.3) * mm, v(-36.76, -29.07) * mm, v(-37.23, -29.48) * mm, v(-37.57, -29.79) * mm, v(-37.76, -29.94) * mm, v(-37.57, -29.94) * mm, v(-37.37, -29.9) * mm, v(-37.12, -30) * mm, v(-36.88, -30.08) * mm, v(-36.6, -30.06) * mm, v(-36.4, -29.94) * mm, v(-36.23, -29.95) * mm, v(-35.95, -30) * mm, v(-35.65, -29.87) * mm, v(-34.64, -29.3) * mm, v(-33.82, -28.87) * mm, v(-33.58, -28.79) * mm, v(-33.42, -28.8) * mm, v(-33.35, -28.95) * mm, v(-33.47, -29.06) * mm, v(-33.76, -29.23) * mm, v(-34.74, -29.64) * mm, v(-35.9, -30.1) * mm, v(-35.99, -30.25) * mm, v(-36.15, -30.38) * mm, v(-36.32, -30.45) * mm, v(-36.45, -30.52) * mm, v(-36.65, -30.48) * mm, v(-36.73, -30.48) * mm, v(-37, -30.6) * mm, v(-37.16, -30.7) * mm, v(-37.42, -30.77) * mm, v(-37.62, -30.86) * mm, v(-37.6, -30.95) * mm, v(-37.57, -31.14) * mm, v(-37.53, -31.29) * mm, v(-37.35, -31.46) * mm, v(-37.15, -31.6) * mm, v(-36.9, -31.92) * mm, v(-36.68, -32.36) * mm, v(-36.62, -32.56) * mm, v(-36.47, -32.84) * mm, v(-36.4, -33) * mm, v(-36.26, -32.9) * mm, v(-35.9, -32.7) * mm, v(-35.66, -32.5) * mm, v(-35.49, -32.31) * mm, v(-35.27, -32.2) * mm, v(-35.1, -32.25) * mm, v(-35, -32.42) * mm, v(-35.1, -32.67) * mm, v(-35.31, -32.94) * mm, v(-35.58, -33.18) * mm, v(-35.93, -33.42) * mm, v(-36.1, -33.53) * mm, v(-36, -33.67) * mm, v(-35.9, -33.92) * mm, v(-35.7, -34.1) * mm, v(-35.4, -34.23) * mm, v(-35.2, -34.31) * mm, v(-34.99, -34.36) * mm, v(-34.99, -34.46) * mm, v(-35.07, -34.56) * mm, v(-35.64, -34.59) * mm, v(-36.04, -34.57) * mm, v(-36.14, -34.59) * mm, v(-36.1, -34.4) * mm, v(-36.1, -34.25) * mm, v(-36.23, -34.13) * mm, v(-36.4, -33.94) * mm, v(-36.57, -33.83) * mm, v(-37.03, -34.03) * mm, v(-37.51, -34.25) * mm, v(-38.19, -34.33) * mm, v(-38.78, -34.4) * mm, v(-39.37, -34.38) * mm, v(-39.57, -34.29) * mm, v(-39.66, -34.53) * mm, v(-39.7, -34.7) * mm, v(-39.92, -34.7) * mm, v(-40.12, -34.67) * mm, v(-40.15, -34.44) * mm, v(-40.07, -34.2) * mm, v(-40.07, -34.07) * mm, v(-40.26, -33.84) * mm, v(-40.47, -33.52) * mm, v(-40.54, -33.33) * mm, v(-40.62, -33.03) * mm, v(-40.65, -32.65) * mm, v(-40.66, -32.52) * mm, v(-40.83, -32.7) * mm, v(-41.6, -33.29) * mm, v(-42.07, -33.67) * mm, v(-42.74, -34) * mm, v(-43.26, -34.18) * mm, v(-44.16, -34.33) * mm, v(-44.85, -34.37) * mm, v(-45.22, -34.31) * mm, v(-45.53, -34.11) * mm, v(-45.68, -33.8) * mm, v(-45.65, -33.45) * mm, v(-45.51, -33.2) * mm, v(-45.2, -32.92) * mm, v(-44.9, -32.75) * mm, v(-44.33, -32.52) * mm, v(-43.93, -32.4) * mm, v(-43.6, -32.4) * mm, v(-43.42, -32.4) * mm, v(-43.33, -32.5) * mm, v(-43.37, -32.68) * mm, v(-43.56, -32.84) * mm, v(-44.06, -32.96) * mm, v(-44.4, -33.15) * mm, v(-44.56, -33.36) * mm, v(-44.31, -33.42) * mm, v(-43.81, -33.38) * mm, v(-43.34, -33.15) * mm, v(-42.74, -32.92) * mm, v(-42.35, -32.63) * mm, v(-41.93, -32.34) * mm, v(-41.62, -32.04) * mm, v(-41.4, -31.75) * mm, v(-41.2, -31.4) * mm, v(-41.15, -31.1) * mm, v(-41.12, -30.76) * mm, v(-41.15, -30.56) * mm, v(-41.31, -30.48) * mm, v(-41.65, -30.4) * mm, v(-41.93, -30.4) * mm, v(-42.15, -30.58) * mm, v(-42.53, -30.84) * mm, v(-42.97, -30.95) * mm, v(-43.24, -30.87) * mm, v(-43.35, -30.6) * mm, v(-43.27, -30.3) * mm, v(-43, -30.08) * mm, v(-42.6, -30) * mm, v(-42.23, -29.95) * mm, v(-41.92, -29.83) * mm, v(-41.1, -29.3) * mm, v(-40.42, -28.81) * mm, v(-40.1, -28.46) * mm, v(-39.96, -28.13) * mm, v(-39.96, -27.9) * mm, v(-40.16, -27.7) * mm, v(-40.57, -27.65) * mm, v(-41.07, -27.65) * mm, v(-41.45, -27.73) * mm, v(-41.72, -27.8) * mm, v(-41.97, -28.07) * mm, v(-42.72, -29.17) * mm, v(-43.53, -30.31) * mm, v(-44.08, -31) * mm, v(-44.97, -32.17) * mm, v(-45.92, -33.4) * mm, v(-46.27, -33.95) * mm, v(-46.37, -34.09) * mm, v(-46.7, -34.25) * mm, v(-47.07, -34.2) * mm, v(-47.26, -34.11) * mm, v(-47.35, -33.92) * mm, v(-47.35, -33.67) * mm, v(-47.14, -33.29) * mm, v(-46.6, -32.58) * mm, v(-45.99, -31.75) * mm, v(-45.6, -31.15) * mm, v(-45.31, -30.83) * mm, v(-45.37, -30.79) * mm, v(-45.7, -30.8) * mm, v(-46.03, -30.8) * mm, v(-46.15, -30.9) * mm, v(-46.34, -31.36) * mm, v(-46.87, -32.36) * mm, v(-47.6, -33.64) * mm, v(-47.92, -34.13) * mm, v(-48.06, -34.29) * mm, v(-48.22, -34.45) * mm, v(-48.49, -34.53) * mm, v(-48.77, -34.59) * mm, v(-49.07, -34.52) * mm, v(-49.24, -34.26) * mm, v(-49.1, -33.73) * mm, v(-48.6, -32.98) * mm, v(-47.9, -31.8) * mm, v(-47.5, -31.1) * mm, v(-47.42, -30.92) * mm, v(-47.64, -30.9) * mm, v(-49.4, -31.23) * mm, v(-49.79, -31.29) * mm, v(-49.97, -31.34) * mm, v(-50.27, -31.75) * mm, v(-51.66, -33.26) * mm, v(-52.02, -33.77) * mm, v(-52.34, -34.2) * mm, v(-52.6, -34.38) * mm, v(-52.93, -34.4) * mm, v(-53.35, -34.25) * mm, v(-53.38, -34) * mm, v(-53.3, -33.77) * mm]});
            skFitSpline(sketch, "E18", {"points": [v(-48.85, -30.37) * mm, v(-47.08, -30.06) * mm, v(-46.95, -30.07) * mm, v(-46.87, -29.95) * mm, v(-46.26, -28.6) * mm, v(-46.18, -28.29) * mm, v(-46.18, -28.11) * mm, v(-46.37, -28.2) * mm, v(-47.53, -29.06) * mm, v(-48.49, -30.02) * mm, v(-48.85, -30.37) * mm]});
            skSolve(sketch);
        }
        {
            var Q0;
            Q0 = qSketchRegion(id + "F9", true);
            extrude(context, id + "F10", {"entities" : qUnion([Q0]), "depth" : 1.52 * mm});
        }
        {
            var Q0;
            {var subQ8=sQuery(id+"F3.wireOp",EDGE,"E14.bottom");var subQ9=makeQuery(id+"F4.opExtrude","SWEPT_FACE",FACE,{"disambiguationData":[OSD([subQ8])]});var subQ60=sQuery(id+"F3.wireOp",EDGE,"E14.top");var subQ68=sQuery(id+"F3.wireOp",EDGE,"E14.left");var subQ75=sQuery(id+"F3.wireOp",EDGE,"E14.right");Q0=makeQuery(id+"F10.boolean.opBoolean","SPLIT",FACE,{"disambiguationData":[TD([subQ9])],"derivedFrom":makeQuery(id+"F6.boolean.opBoolean","SPLIT",FACE,{"disambiguationData":[TD([subQ9])],"derivedFrom":makeQuery(id+"F4.opExtrude","CAP_FACE",FACE,{"disambiguationData":[OSD([subQ8,subQ60,subQ68,subQ75])],"isStart":true})})});}
            var sketch = newSketch(context, id + "F11", { "sketchPlane" : qUnion([Q0])});
            skFitSpline(sketch, "E19.0", {"points": [v(-11.39, 9.52) * mm, v(-11.25, 9.24) * mm, v(-9.78, 8.3) * mm, v(-8.5, 7.6) * mm, v(-8.28, 7.38) * mm, v(-8.12, 7) * mm, v(-6.87, 5.34) * mm, v(-6.68, 5.01) * mm, v(-6.25, 5.17) * mm, v(-4.54, 5.3) * mm, v(-3.53, 5.34) * mm, v(-1.83, 5.03) * mm, v(1.45, 4.47) * mm, v(3.35, 4.05) * mm, v(5.89, 3.47) * mm, v(6.03, 3.34) * mm, v(6.26, 3.54) * mm, v(6.88, 3.83) * mm, v(7.22, 4.01) * mm, v(7.28, 4.28) * mm, v(7.02, 4.49) * mm, v(6.64, 4.93) * mm, v(6.2, 5.4) * mm, v(6.06, 5.61) * mm, v(5.77, 5.74) * mm, v(3.77, 6.17) * mm, v(3.12, 6.64) * mm, v(2.16, 6.87) * mm, v(1.27, 7.5) * mm, v(0.72, 7.8) * mm, v(0.11, 7.92) * mm, v(-0.25, 8.04) * mm, v(-2.76, 7.93) * mm, v(-3.99, 7.98) * mm, v(-4.29, 7.89) * mm, v(-4.5, 8.05) * mm, v(-5.33, 8.36) * mm, v(-6.3, 8.63) * mm, v(-6.42, 8.8) * mm, v(-8.35, 8.59) * mm, v(-8.75, 9.04) * mm, v(-9.32, 9.23) * mm, v(-9.93, 9.58) * mm, v(-10.61, 9.62) * mm, v(-11.13, 9.69) * mm, v(-11.4, 9.74) * mm, v(-11.43, 9.6) * mm, v(-11.39, 9.52) * mm]});
            skFitSpline(sketch, "E20", {"points": [v(13.74, 19.88) * mm, v(14.35, 20.52) * mm, v(14.93, 20.98) * mm, v(15.4, 21.3) * mm, v(15.76, 21.57) * mm, v(16, 21.9) * mm, v(16.12, 22) * mm, v(16.39, 22.08) * mm, v(16.49, 22.23) * mm, v(16.52, 22.53) * mm, v(16.62, 22.76) * mm, v(16.79, 22.91) * mm, v(16.8, 23.21) * mm, v(16.7, 23.63) * mm, v(17.1, 24.24) * mm, v(17.33, 24.56) * mm, v(17.53, 24.92) * mm, v(18, 25.32) * mm, v(18.34, 25.46) * mm, v(18.64, 25.73) * mm, v(18.85, 25.86) * mm, v(18.92, 26.08) * mm, v(19.27, 26.35) * mm, v(19.62, 26.54) * mm, v(19.62, 26.94) * mm, v(19.91, 27.05) * mm, v(20.67, 27.9) * mm, v(20.57, 28.3) * mm, v(20.88, 28.6) * mm, v(21.36, 29.1) * mm, v(21.43, 29.43) * mm, v(21.51, 29.77) * mm, v(21.81, 29.94) * mm, v(22.13, 30.2) * mm, v(22.17, 30.5) * mm, v(22.23, 31.02) * mm, v(22.33, 31.32) * mm, v(22.66, 31.55) * mm, v(22.83, 31.73) * mm, v(22.93, 32.22) * mm, v(22.9, 32.72) * mm, v(22.92, 33.04) * mm, v(23.16, 33.25) * mm, v(23.39, 33.57) * mm, v(23.49, 33.7) * mm], "startDerivative": vector(17.89, 19.84) * mm, "endDerivative": vector(6.14, 8.22) * mm});
            skFitSpline(sketch, "E21", {"points": [v(23.49, 33.7) * mm, v(23.23, 34) * mm, v(23.27, 34.2) * mm, v(23.49, 34.5) * mm, v(23.49, 34.55) * mm, v(23.09, 34.8) * mm, v(22.52, 35.18) * mm, v(21.89, 35.56) * mm, v(21.4, 35.91) * mm, v(21.16, 36.17) * mm, v(20.8, 36.39) * mm, v(20.37, 36.62) * mm, v(20.02, 36.79) * mm, v(19.52, 36.92) * mm, v(19.17, 36.93) * mm, v(18.85, 36.82) * mm, v(18.66, 36.64) * mm, v(18.54, 36.44) * mm, v(18.3, 36.21) * mm, v(18.03, 36.1) * mm, v(17.68, 36.1) * mm, v(17.52, 36.21) * mm, v(17.3, 36.19) * mm, v(16.92, 36.07) * mm, v(16.63, 36.16) * mm, v(16.39, 36.4) * mm, v(16.35, 36.67) * mm, v(16.33, 36.9) * mm, v(16.27, 37.22) * mm, v(16.24, 37.47) * mm, v(16.24, 37.8) * mm, v(16.49, 38.23) * mm, v(16.77, 38.45) * mm, v(17.02, 38.5) * mm, v(17.35, 38.5) * mm, v(17.65, 38.4) * mm, v(17.96, 38.3) * mm, v(18.1, 38.08) * mm, v(18.1, 37.93) * mm, v(18.16, 37.78) * mm, v(18.3, 37.9) * mm, v(18.48, 38.02) * mm, v(18.74, 38.1) * mm, v(19.07, 38.12) * mm, v(19.45, 38.06) * mm, v(20.5, 37.85) * mm, v(21.23, 37.63) * mm, v(22.26, 37.39) * mm, v(23, 37.09) * mm, v(23.66, 36.79) * mm, v(24, 36.59) * mm, v(24.42, 36.33) * mm, v(24.74, 36.19) * mm, v(25.02, 36.07) * mm, v(25.02, 36.29) * mm, v(24.92, 36.63) * mm, v(24.92, 37.19) * mm, v(24.94, 37.42) * mm, v(25.08, 37.82) * mm, v(25.32, 38.13) * mm, v(25.64, 38.42) * mm, v(25.92, 38.63) * mm, v(26.25, 38.8) * mm, v(26.45, 38.85) * mm, v(26.78, 38.9) * mm, v(27.27, 38.92) * mm, v(27.84, 38.8) * mm, v(28.39, 38.45) * mm, v(28.66, 38.13) * mm, v(28.72, 37.9) * mm, v(28.86, 37.69) * mm, v(29.27, 37.62) * mm, v(29.57, 37.57) * mm, v(30, 37.5) * mm, v(30.3, 37.45) * mm, v(30.42, 37.3) * mm, v(30.5, 37.1) * mm, v(30.36, 37.02) * mm, v(29.89, 36.84) * mm, v(29.6, 36.83) * mm, v(29.25, 36.73) * mm, v(28.99, 36.67) * mm, v(28.93, 36.47) * mm, v(29.07, 36.31) * mm, v(29.19, 36.1) * mm, v(29.25, 35.93) * mm, v(29.1, 35.76) * mm, v(29, 35.63) * mm, v(28.93, 35.48) * mm, v(28.96, 35.37) * mm, v(28.9, 35.2) * mm, v(28.79, 35.11) * mm, v(28.69, 35) * mm, v(28.73, 34.9) * mm, v(28.87, 34.8) * mm, v(28.76, 34.63) * mm, v(28.63, 34.4) * mm, v(28.59, 34.25) * mm, v(28.59, 34.08) * mm, v(28.54, 33.98) * mm, v(28.44, 33.88) * mm, v(28.24, 33.7) * mm, v(27.87, 33.7) * mm, v(27.6, 33.7) * mm, v(27.47, 33.4) * mm, v(27.36, 33.2) * mm, v(27.36, 33) * mm, v(27.31, 32.74) * mm, v(27.34, 32.53) * mm, v(27.46, 32.4) * mm, v(27.67, 32.28) * mm, v(27.71, 32.06) * mm, v(27.86, 31.75) * mm, v(28.03, 31.29) * mm, v(28.16, 30.92) * mm, v(28.36, 30.53) * mm, v(28.53, 30.07) * mm, v(28.62, 29.63) * mm, v(28.46, 28.57) * mm, v(28.44, 28.13) * mm, v(28.4, 27.85) * mm, v(28.34, 27.44) * mm, v(28.19, 27) * mm, v(28.1, 26.66) * mm, v(28.04, 26.38) * mm, v(28.4, 26.25) * mm, v(28.74, 26.13) * mm, v(29.22, 26.06) * mm, v(29.65, 26.05) * mm, v(30.1, 26.05) * mm, v(30.5, 26.06) * mm, v(30.76, 26.02) * mm, v(30.78, 25.7) * mm, v(30.78, 25.32) * mm, v(30.76, 24.95) * mm, v(30.55, 24.63) * mm, v(30.28, 24.36) * mm, v(29.89, 24.09) * mm, v(29.69, 23.79) * mm, v(29.47, 23.64) * mm, v(29.03, 23.8) * mm, v(28.72, 23.94) * mm, v(28.4, 24.04) * mm, v(27.97, 24.13) * mm, v(27.7, 24.23) * mm, v(27.28, 24.35) * mm, v(27, 24.53) * mm, v(26.61, 24.67) * mm, v(26.31, 24.77) * mm, v(26.1, 24.69) * mm, v(25.87, 24.47) * mm, v(25.72, 24.33) * mm, v(27.6, 23.72) * mm, v(28.4, 23.41) * mm, v(29.49, 22.74) * mm, v(30, 22.34) * mm, v(30.5, 22.1) * mm, v(30.95, 21.84) * mm, v(31.02, 21.44) * mm, v(30.98, 20.7) * mm, v(31.06, 20.16) * mm, v(31.2, 19.7) * mm, v(31.25, 19.15) * mm, v(31.4, 18.03) * mm, v(31.45, 16.99) * mm, v(31.55, 16.04) * mm, v(31.54, 15.22) * mm, v(31.68, 14.65) * mm, v(31.7, 14.3) * mm, v(31.94, 13.92) * mm, v(32.02, 13.4) * mm, v(32.05, 12.92) * mm, v(32.47, 12.58) * mm, v(33.14, 12.07) * mm, v(33.58, 11.6) * mm, v(34.31, 11.13) * mm, v(34.94, 10.79) * mm, v(35.43, 10.49) * mm, v(35.56, 10.23) * mm, v(35.53, 9.86) * mm, v(35.19, 9.64) * mm, v(34.59, 9.55) * mm, v(34.03, 9.61) * mm, v(33.44, 9.75) * mm, v(32.93, 9.87) * mm, v(32.61, 9.58) * mm, v(32.62, 9.97) * mm, v(32.3, 10.07) * mm, v(31.88, 10.14) * mm, v(31.5, 10.18) * mm, v(31.15, 10.26) * mm, v(30.96, 10) * mm, v(30.73, 10.27) * mm, v(30.53, 10.26) * mm, v(30.2, 10.3) * mm, v(29.96, 10.3) * mm, v(29.69, 10.27) * mm, v(29.45, 10.49) * mm, v(29.15, 10.59) * mm, v(28.86, 10.5) * mm, v(28.86, 10.76) * mm, v(28.9, 11.46) * mm, v(29.05, 11.99) * mm, v(29.19, 12.23) * mm, v(29.32, 12.53) * mm, v(29.52, 12.8) * mm, v(29.46, 12.96) * mm, v(29.5, 13.22) * mm, v(29.55, 13.55) * mm, v(29.29, 14.35) * mm, v(29.13, 15.15) * mm, v(29.02, 15.61) * mm, v(28.87, 16.23) * mm, v(28.44, 16.87) * mm, v(28.26, 17.36) * mm, v(28.19, 18.22) * mm, v(28.17, 18.78) * mm, v(28.14, 19.3) * mm, v(28.06, 19.73) * mm, v(27.76, 19.8) * mm, v(27.16, 19.8) * mm, v(26.78, 19.8) * mm, v(26.44, 19.9) * mm, v(25.9, 19.86) * mm, v(25.1, 19.78) * mm, v(24.32, 19.76) * mm, v(23.22, 19.75) * mm, v(22.56, 19.83) * mm], "startDerivative": vector(-76.94, 71.94) * mm, "endDerivative": vector(-105.06, 19.2) * mm});
            skFitSpline(sketch, "E22", {"points": [v(13.74, 19.88) * mm, v(13.3, 19.47) * mm, v(12.92, 19.08) * mm, v(12.52, 19.02) * mm, v(12.38, 18.8) * mm, v(12.05, 18.74) * mm, v(11.65, 18.74) * mm, v(11.43, 18.64) * mm, v(10.96, 18.6) * mm, v(9.64, 18.55) * mm, v(8.6, 18.17) * mm, v(7.27, 17.38) * mm, v(7.09, 17.26) * mm, v(6.7, 17.26) * mm, v(6.32, 17.22) * mm, v(5.98, 16.95) * mm, v(5.47, 16.79) * mm, v(4.93, 16.79) * mm, v(4.54, 17.14) * mm, v(4.05, 17.64) * mm, v(3.61, 17.64) * mm, v(3.04, 17.52) * mm, v(3.06, 17.28) * mm, v(2.78, 17.26) * mm, v(2.84, 16.99) * mm, v(2.52, 16.93) * mm, v(2.48, 16.43) * mm, v(2.15, 16.45) * mm, v(2.13, 15.88) * mm, v(1.85, 15.62) * mm, v(1.42, 15.54) * mm, v(0.77, 14.8) * mm, v(0.49, 14.2) * mm, v(0.21, 13.4) * mm, v(0.23, 12.84) * mm, v(0.35, 12.66) * mm, v(0.73, 12.6) * mm, v(1.36, 12.72) * mm, v(1.85, 12.97) * mm, v(2.46, 13.11) * mm, v(2.74, 13.21) * mm, v(3, 13.35) * mm, v(3.47, 13.33) * mm, v(3.93, 13.5) * mm, v(4.34, 13.78) * mm, v(4.24, 13.88) * mm, v(4.03, 14.04) * mm, v(4.26, 14.24) * mm, v(4.78, 14.42) * mm, v(5.3, 14.63) * mm, v(5.6, 14.56) * mm, v(6.26, 14.83) * mm, v(7.09, 14.93) * mm, v(7.36, 15.23) * mm, v(7.84, 15.13) * mm, v(8.41, 15.3) * mm, v(9.62, 15.46) * mm, v(10.55, 15.72) * mm, v(11.24, 15.86) * mm, v(11.83, 15.98) * mm, v(12.42, 16) * mm, v(12.94, 16) * mm, v(13.25, 16.18) * mm, v(13.74, 16.21) * mm, v(14.28, 16.47) * mm, v(14.61, 16.7) * mm, v(15.2, 16.73) * mm, v(16.16, 17.12) * mm, v(17.7, 17.91) * mm, v(19.4, 18.88) * mm, v(20.92, 19.7) * mm, v(21.23, 19.88) * mm, v(21.45, 20.1) * mm, v(21.75, 20.1) * mm, v(22.56, 19.83) * mm], "startDerivative": vector(-33.53, -25.64) * mm, "endDerivative": vector(53.13, -18.96) * mm});
            skSolve(sketch);
        }
        {
            var Q0;
            Q0 = qSketchRegion(id + "F11", true);
            extrude(context, id + "F12", {"entities" : qUnion([Q0]), "depth" : 1.52 * mm});
        }
        {
            var Q0;
            {var subQ8=sQuery(id+"F3.wireOp",EDGE,"E14.bottom");var subQ9=makeQuery(id+"F4.opExtrude","SWEPT_FACE",FACE,{"disambiguationData":[OSD([subQ8])]});var subQ60=sQuery(id+"F3.wireOp",EDGE,"E14.top");var subQ68=sQuery(id+"F3.wireOp",EDGE,"E14.left");var subQ75=sQuery(id+"F3.wireOp",EDGE,"E14.right");Q0=makeQuery(id+"F10.boolean.opBoolean","SPLIT",FACE,{"disambiguationData":[TD([subQ9])],"derivedFrom":makeQuery(id+"F6.boolean.opBoolean","SPLIT",FACE,{"disambiguationData":[TD([subQ9])],"derivedFrom":makeQuery(id+"F4.opExtrude","CAP_FACE",FACE,{"disambiguationData":[OSD([subQ8,subQ60,subQ68,subQ75])],"isStart":true})})});}
            var sketch = newSketch(context, id + "F13", { "sketchPlane" : qUnion([Q0])});
            skCircle(sketch, "E23", {"center": v(0, 34.93) * mm, "radius": 1.59 * mm});
            skSolve(sketch);
        }
        {
            var Q0;
            Q0 = qSketchRegion(id + "F13", true);
            extrude(context, id + "F14", {"entities" : qUnion([Q0]), "operationType" : NewBodyOperationType.REMOVE, "endBound" : BoundingType.THROUGH_ALL, "oppositeDirection" : true, "depth" : 25.4 * mm});
        }
        {
            var Q0;
            Q0=makeQuery(id+"F10.opExtrude","SWEPT_BODY",BODY,{"disambiguationData":[OSD([sQuery(id+"F9.wireOp",EDGE,"E17"),sQuery(id+"F9.wireOp",EDGE,"E18")])]});
            var Q1;
            Q1=qCreatedBy(makeId("Origin.pointOp"),VERTEX);
            transform(context, id + "F15", {"entities" : qUnion([Q0]), "transformType" : TransformType.SCALE_UNIFORMLY, "scale" : 2, "scalePoint" : qUnion([Q1]), "makeCopy" : false});
        }
        {
            var Q0;
            Q0=makeQuery(id+"F8.opExtrude","SWEPT_BODY",BODY,{"disambiguationData":[OSD([sQuery(id+"F7.wireOp",EDGE,"E16")])]});
            var Q1;
            Q1=makeQuery(id+"F12.opExtrude","SWEPT_BODY",BODY,{"disambiguationData":[OSD([sQuery(id+"F11.wireOp",EDGE,"E20"),sQuery(id+"F11.wireOp",EDGE,"E21"),sQuery(id+"F11.wireOp",EDGE,"E22")])]});
            var Q2;
            Q2=qCreatedBy(makeId("Origin.pointOp"),VERTEX);
            transform(context, id + "F16", {"entities" : qUnion([Q0, Q1]), "transformType" : TransformType.SCALE_UNIFORMLY, "scale" : 1.5, "scalePoint" : qUnion([Q2]), "makeCopy" : false});
        }
    });
